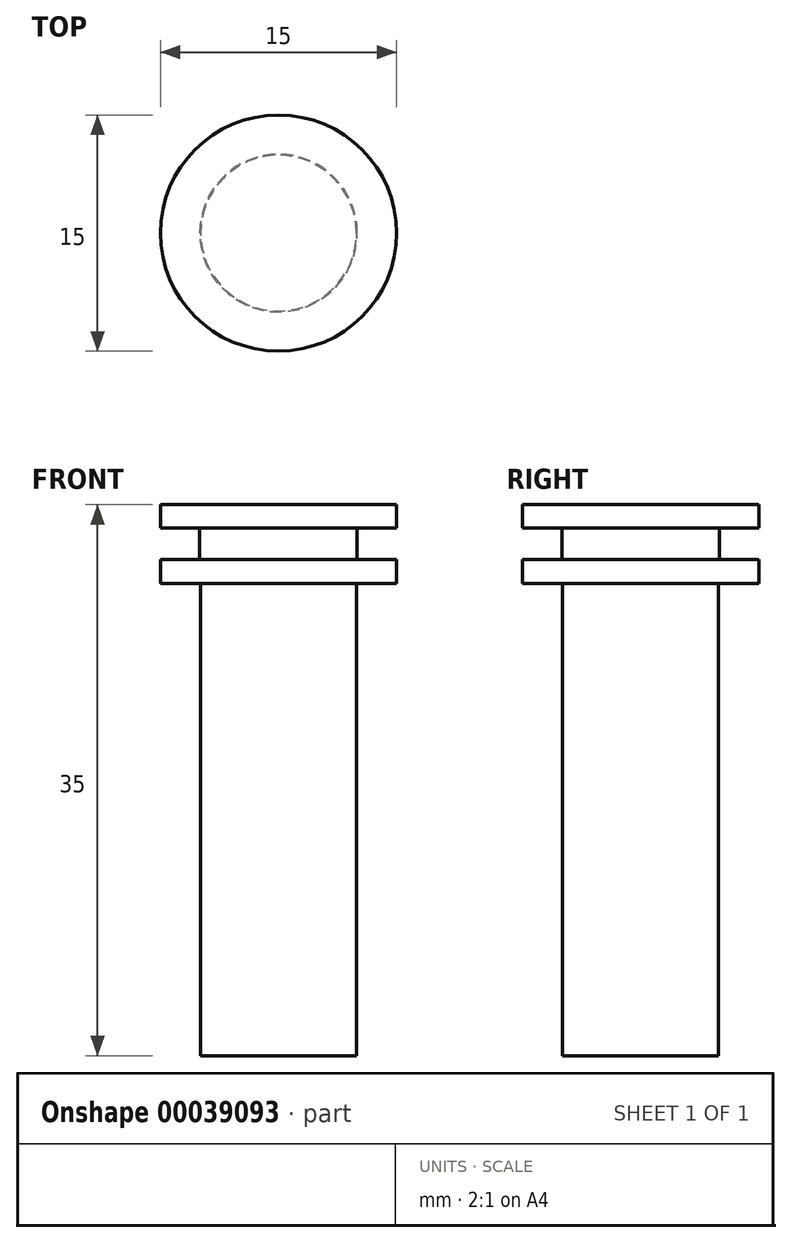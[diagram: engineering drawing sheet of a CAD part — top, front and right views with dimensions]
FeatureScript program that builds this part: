
annotation { "Feature Type Name" : "Feature", "Feature Type Description" : "" }
export const myFeature = defineFeature(function(context is Context, id is Id, definition is map)
    precondition{}
    {
        {
            var Q0;
            Q0=qCreatedBy(makeId("Top.planeOp"),FACE);
            var sketch = newSketch(context, id + "F0", { "sketchPlane" : qUnion([Q0])});
            skCircle(sketch, "E0", {"center": v(0, 0) * mm, "radius": 7.5 * mm});
            skSolve(sketch);
        }
        {
            var Q0;
            Q0=makeQuery(id+"F0.imprint","IMPRINT",FACE,{"disambiguationData":[TD([[makeQuery(id+"F0.imprint","IMPRINT",EDGE,{"derivedFrom":sQuery(id+"F0.wireOp",EDGE,"E0")}),1.0]])]});
            extrude(context, id + "F1", {"entities" : qUnion([Q0]), "oppositeDirection" : true, "depth" : 2.5 * mm, "hasSecondDirection" : true, "secondDirectionOppositeDirection" : false, "secondDirectionDepth" : 2.5 * mm});
        }
        {
            var Q0;
            Q0=makeQuery(id+"F1.opExtrude","CAP_FACE",FACE,{"disambiguationData":[OSD([sQuery(id+"F0.wireOp",EDGE,"E0")])],"isStart":false});
            var sketch = newSketch(context, id + "F2", { "sketchPlane" : qUnion([Q0])});
            skCircle(sketch, "E1", {"center": v(0, 0) * mm, "radius": 4.95 * mm});
            skSolve(sketch);
        }
        {
            var Q0;
            Q0=makeQuery(id+"F2.imprint","IMPRINT",FACE,{"disambiguationData":[TD([[makeQuery(id+"F2.imprint","IMPRINT",EDGE,{"derivedFrom":sQuery(id+"F2.wireOp",EDGE,"E1")}),1.0]])]});
            extrude(context, id + "F3", {"entities" : qUnion([Q0]), "operationType" : NewBodyOperationType.ADD, "depth" : 30 * mm});
        }
        {
            var Q0;
            Q0=qCreatedBy(makeId("Top.planeOp"),FACE);
            var sketch = newSketch(context, id + "F4", { "sketchPlane" : qUnion([Q0])});
            skCircle(sketch, "E2", {"center": v(0, 0) * mm, "radius": 5 * mm});
            skCircle(sketch, "E3", {"center": v(0, 0) * mm, "radius": 7.55 * mm});
            skSolve(sketch);
        }
        {
            var Q0;
            Q0 = qSketchRegion(id + "F4", true);
            extrude(context, id + "F5", {"entities" : qUnion([Q0]), "operationType" : NewBodyOperationType.REMOVE, "oppositeDirection" : true, "depth" : 1 * mm, "hasSecondDirection" : true, "secondDirectionOppositeDirection" : false, "secondDirectionDepth" : 1 * mm});
        }
    });
